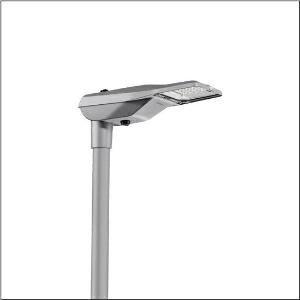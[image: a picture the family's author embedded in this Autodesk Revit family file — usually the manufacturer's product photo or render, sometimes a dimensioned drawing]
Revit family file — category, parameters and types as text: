
# Revit family: streetlight_sl_21_micro___st1_5a_5xe1p43t08db_e62a
name_source: partatom
category: Lighting Fixtures
units: mm (PartAtom-declared; Revit-internal decimal feet)

## family parameters
Cut with Voids When Loaded = No
Host = Face
Light Source = No
Part Type = Normal
Room Calculation Point = No
Round Connector Dimension = Use Diameter
Shared = No

## types (1)
- --- (1 x LED, 5230 lm, 39.1 W, 4000K)
    Apparent Load = 39 VA
    CIE Flux Codes = 22 53 95 100 100
    Color Rendering = 70
    Color Temperature = 4000K
    Default Elevation = 1800 mm
    Description = Streetlight SL 21 micro, mast luminaire, primary light control with lens, of PMMA, primary optical cover: cover, of toughened safety glass, transparent, light distribution: ST1.5a, light emission: direct distribution, primary light characteristic: asymmetric, installation type: side-entry, post-top, LED, High Power LED, rated luminous flux: 5.230lm, luminous efficacy: 134lm/W, light colour: 740, colour temperature: 4000K, control: flexible luminous flux parameterisation, time-dependent luminous flux control, constant luminous flux control, overheat protection, pre-setting: logarithmic dimming characteristic, mains connection: 220..240V, AC, 50/60Hz, start of lifetime: 39W, end of service life: 41W, reduction: 18W, luminaire housing, of diecast aluminium, powder-coated, Siteco® metallic grey (DB 702S), corrosivity category C5 mid according to DIN EN ISO 12944, please order mast flange separately, inclination adjustable: 0°, 5°, 10°, 15°, sealing non-destructively replaceable, multi-level sealing system, length: 528mm, width: 235mm, height: 110mm, mast flange for spigot size: 42mm (side-entry): 5XC10008XM4, 60/48mm (side-entry/post-top): 5XC10108XM2, 76/60mm (side-entry/post-top): 5XC10108XM1, Smart Interface below and above, protection rating (complete): IP66, insulation class (complete): insulation class II (safety insulation), certification: CE, ENEC, ENEC+, VDE, impact resistance: IK09, permissible operating ambient temperature for outdoor applications: -40..+50°C, standard-compliant lighting for roads and squares, packaging unit: 1 piece

Light Distribution: ST1.5a
    Height = 110 mm
    Lamp = 1 x LED
    Lamp Light Flux = 5230 lm
    Lamp Power = 39.1 W
    Lamp count = 1
    Length = 528 mm
    Luminous efficacy = 134 lm/W
    Manufacturer = Siteco
    ModVariant = No
    Model = 5XE1P43T08DB
    Number of Poles = 1
    OnlyDefault = Yes
    Power Factor = 1
    Product Name = Streetlight SL 21 micro | ST1.5a
    Product group = mast luminaire | pylon top
    ProductGroupID = 6100
    Protection Class = Protection class II
    Protection Degree = IP 66
    RLX_Detail_Level = 1
    RLX_Emergency_Light_Flux = 0 lm
    RLX_Emergency_Type = 0
    RLX_Emergency_Type_DB = No
    RlxData = <blob elided: 102301 chars, md5=189947ef>
    Socket = socket
    Standby Power = 0 W
    System Light Flux = 5230 lm
    System Power = 39 W
    Type Comments = factory setting: luminous flux: 100 % | dim-lin: 254 | 765 mA
    Type Image = l_1007239.jpg
    URL = http://relux.com
    VarID = @adj_124007
    Voltage = 0 V
    Weight = 0.00 kg
    Width = 235 mm

## geometry (parser evidence)
native form markers: Blend x4, Sweep x12
no freeform markers — native parametric forms only
